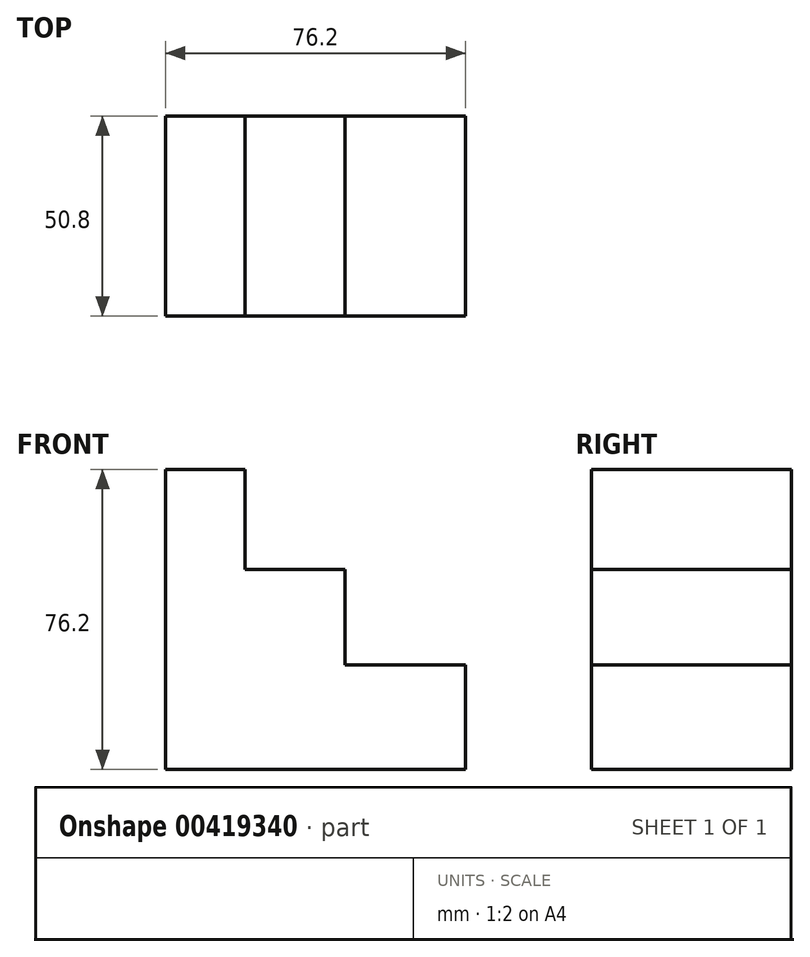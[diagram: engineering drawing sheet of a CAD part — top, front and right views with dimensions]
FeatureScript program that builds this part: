
annotation { "Feature Type Name" : "Feature", "Feature Type Description" : "" }
export const myFeature = defineFeature(function(context is Context, id is Id, definition is map)
    precondition{}
    {
        {
            var Q0;
            Q0=qCreatedBy(makeId("Front.planeOp"),FACE);
            var sketch = newSketch(context, id + "F0", { "sketchPlane" : qUnion([Q0])});
            skLineSegment(sketch, "E0", {"start": v(0, 0) * mm, "end": v(-76.2, 0) * mm});
            skLineSegment(sketch, "E1", {"start": v(-76.2, 0) * mm, "end": v(-76.2, 76.2) * mm});
            skLineSegment(sketch, "E2", {"start": v(-76.2, 76.2) * mm, "end": v(-55.95, 76.2) * mm});
            skLineSegment(sketch, "E3", {"start": v(-55.95, 76.2) * mm, "end": v(-55.95, 50.8) * mm});
            skLineSegment(sketch, "E4", {"start": v(-55.95, 50.8) * mm, "end": v(-30.55, 50.8) * mm});
            skLineSegment(sketch, "E5", {"start": v(-30.55, 50.8) * mm, "end": v(-30.55, 26.54) * mm});
            skLineSegment(sketch, "E6", {"start": v(-30.55, 26.54) * mm, "end": v(-5.15, 26.54) * mm});
            skLineSegment(sketch, "E7", {"start": v(-5.15, 26.54) * mm, "end": v(0, 26.54) * mm});
            skLineSegment(sketch, "E8", {"start": v(0, 26.54) * mm, "end": v(0, 0) * mm});
            skSolve(sketch);
        }
        {
            var Q0;
            Q0 = qSketchRegion(id + "F0", true);
            extrude(context, id + "F1", {"entities" : qUnion([Q0]), "depth" : 50.8 * mm});
        }
    });
